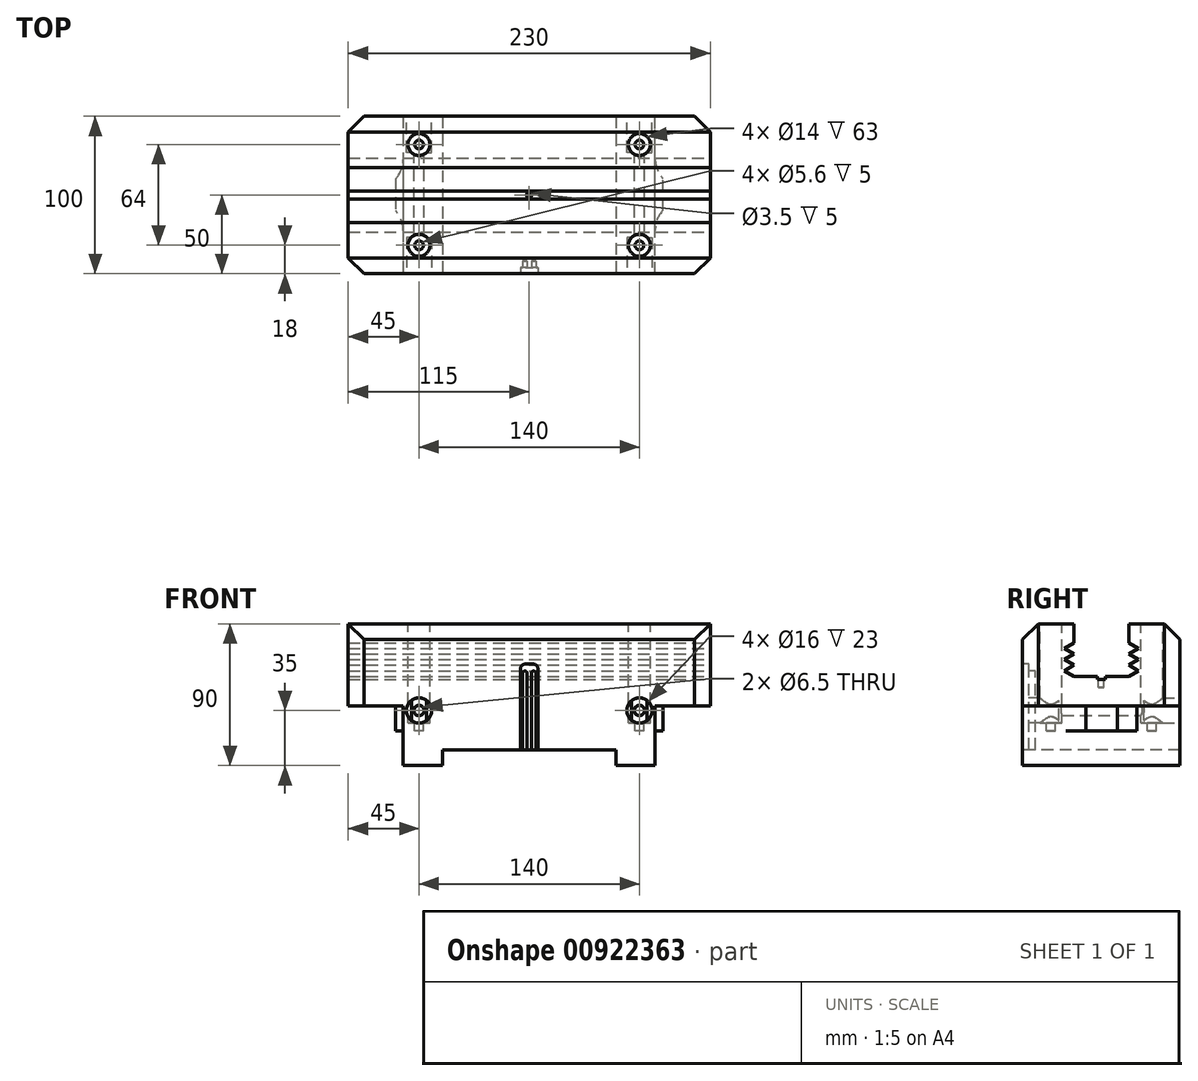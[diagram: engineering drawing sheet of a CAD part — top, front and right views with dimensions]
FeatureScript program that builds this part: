
annotation { "Feature Type Name" : "Feature", "Feature Type Description" : "" }
export const myFeature = defineFeature(function(context is Context, id is Id, definition is map)
    precondition{}
    {
        {
            var Q0;
            Q0=qCreatedBy(makeId("Top.planeOp"),FACE);
            var sketch = newSketch(context, id + "F0", { "sketchPlane" : qUnion([Q0])});
            skLineSegment(sketch, "E0.bottom", {"start": v(-115, 50) * mm, "end": v(115, 50) * mm});
            skLineSegment(sketch, "E0.top", {"start": v(-115, -50) * mm, "end": v(115, -50) * mm});
            skLineSegment(sketch, "E0.left", {"start": v(-115, 50) * mm, "end": v(-115, -50) * mm});
            skLineSegment(sketch, "E0.right", {"start": v(115, 50) * mm, "end": v(115, -50) * mm});
            skSolve(sketch);
        }
        {
            var Q0;
            Q0=makeQuery(id+"F0.imprint","IMPRINT",FACE,{"disambiguationData":[TD([[makeQuery(id+"F0.imprint","IMPRINT",EDGE,{"derivedFrom":sQuery(id+"F0.wireOp",EDGE,"E0.bottom")}),-1.0]])]});
            extrude(context, id + "F1", {"entities" : qUnion([Q0]), "oppositeDirection" : true, "depth" : 52 * mm, "offsetDistance" : 25 * mm});
        }
        {
            var Q0;
            Q0=makeQuery(id+"F1.opExtrude","SWEPT_FACE",FACE,{"disambiguationData":[OSD([sQuery(id+"F0.wireOp",EDGE,"E0.right")])]});
            var sketch = newSketch(context, id + "F2", { "sketchPlane" : qUnion([Q0])});
            skLineSegment(sketch, "E1", {"start": v(-17.5, 0) * mm, "end": v(17.5, 0) * mm});
            skLineSegment(sketch, "E2", {"start": v(-17.5, 0) * mm, "end": v(-17.5, -12) * mm});
            skLineSegment(sketch, "E3", {"start": v(-17.5, -12) * mm, "end": v(-23.52, -15.55) * mm});
            skLineSegment(sketch, "E4", {"start": v(-23.52, -15.55) * mm, "end": v(-17.5, -19.1) * mm});
            skLineSegment(sketch, "E5", {"start": v(-17.5, -19.1) * mm, "end": v(-23.52, -22.65) * mm});
            skLineSegment(sketch, "E6", {"start": v(-23.52, -22.65) * mm, "end": v(-17.5, -26.2) * mm});
            skLineSegment(sketch, "E7", {"start": v(-17.5, -26.2) * mm, "end": v(-23.52, -29.75) * mm});
            skLineSegment(sketch, "E8", {"start": v(-23.52, -29.75) * mm, "end": v(-17.5, -33.3) * mm});
            skLineSegment(sketch, "E9", {"start": v(17.5, 0) * mm, "end": v(17.5, -12) * mm});
            skLineSegment(sketch, "E10", {"start": v(17.5, -33.3) * mm, "end": v(23.52, -29.75) * mm});
            skLineSegment(sketch, "E11", {"start": v(23.52, -29.75) * mm, "end": v(17.5, -26.2) * mm});
            skLineSegment(sketch, "E12", {"start": v(17.5, -26.2) * mm, "end": v(23.52, -22.65) * mm});
            skLineSegment(sketch, "E13", {"start": v(23.52, -22.65) * mm, "end": v(17.5, -19.1) * mm});
            skLineSegment(sketch, "E14", {"start": v(17.5, -19.1) * mm, "end": v(23.52, -15.55) * mm});
            skLineSegment(sketch, "E15", {"start": v(23.52, -15.55) * mm, "end": v(17.5, -12) * mm});
            skLineSegment(sketch, "E16", {"start": v(-17.5, -33.3) * mm, "end": v(-2.5, -33.3) * mm});
            skLineSegment(sketch, "E17", {"start": v(17.5, -33.3) * mm, "end": v(2.5, -33.3) * mm});
            skLineSegment(sketch, "E18", {"start": v(-2.5, -33.3) * mm, "end": v(-2.5, -35.3) * mm});
            skLineSegment(sketch, "E19", {"start": v(2.5, -33.3) * mm, "end": v(2.5, -35.3) * mm});
            skLineSegment(sketch, "E20", {"start": v(2.5, -35.3) * mm, "end": v(-2.5, -35.3) * mm});
            skSolve(sketch);
        }
        {
            var Q0;
            Q0=makeQuery(id+"F2.imprint","IMPRINT",FACE,{"disambiguationData":[TD([[makeQuery(id+"F2.imprint","IMPRINT",EDGE,{"derivedFrom":sQuery(id+"F2.wireOp",EDGE,"E1")}),1.0]])]});
            extrude(context, id + "F3", {"entities" : qUnion([Q0]), "operationType" : NewBodyOperationType.REMOVE, "endBound" : BoundingType.UP_TO_NEXT, "oppositeDirection" : true, "depth" : 218 * mm, "offsetDistance" : 25 * mm});
        }
        {
            var Q0;
            Q0=makeQuery(id+"F1.opExtrude","CAP_EDGE",EDGE,{"disambiguationData":[OSD([sQuery(id+"F0.wireOp",EDGE,"E0.bottom")])],"isStart":true});
            var Q1;
            Q1=makeQuery(id+"F1.opExtrude","CAP_EDGE",EDGE,{"disambiguationData":[OSD([sQuery(id+"F0.wireOp",EDGE,"E0.top")])],"isStart":true});
            var Q2;
            Q2=makeQuery(id+"F1.opExtrude","SWEPT_EDGE",EDGE,{"disambiguationData":[OSD([sQuery(id+"F0.wireOp",EDGE,"E0.top"),sQuery(id+"F0.wireOp",EDGE,"E0.right")])]});
            var Q3;
            Q3=makeQuery(id+"F1.opExtrude","SWEPT_EDGE",EDGE,{"disambiguationData":[OSD([sQuery(id+"F0.wireOp",EDGE,"E0.bottom"),sQuery(id+"F0.wireOp",EDGE,"E0.right")])]});
            var Q4;
            Q4=makeQuery(id+"F1.opExtrude","SWEPT_EDGE",EDGE,{"disambiguationData":[OSD([sQuery(id+"F0.wireOp",EDGE,"E0.top"),sQuery(id+"F0.wireOp",EDGE,"E0.left")])]});
            var Q5;
            Q5=makeQuery(id+"F1.opExtrude","SWEPT_EDGE",EDGE,{"disambiguationData":[OSD([sQuery(id+"F0.wireOp",EDGE,"E0.bottom"),sQuery(id+"F0.wireOp",EDGE,"E0.left")])]});
            chamfer(context, id + "F4", {"entities" : qUnion([Q0, Q1, Q2, Q3, Q4, Q5]), "width" : 10 * mm, "tangentPropagation" : true});
        }
        {
            var Q0;
            Q0=makeQuery(id+"F1.opExtrude","CAP_FACE",FACE,{"disambiguationData":[OSD([sQuery(id+"F0.wireOp",EDGE,"E0.bottom"),sQuery(id+"F0.wireOp",EDGE,"E0.top"),sQuery(id+"F0.wireOp",EDGE,"E0.left"),sQuery(id+"F0.wireOp",EDGE,"E0.right")])],"isStart":false});
            var sketch = newSketch(context, id + "F5", { "sketchPlane" : qUnion([Q0])});
            skLineSegment(sketch, "E21", {"start": v(80, 50) * mm, "end": v(80, -50) * mm});
            skLineSegment(sketch, "E22", {"start": v(80, -50) * mm, "end": v(-80, -50) * mm});
            skLineSegment(sketch, "E23", {"start": v(-80, -50) * mm, "end": v(-80, 50) * mm});
            skLineSegment(sketch, "E24", {"start": v(-80, 50) * mm, "end": v(80, 50) * mm});
            skSolve(sketch);
        }
        {
            var Q0;
            Q0=makeQuery(id+"F5.imprint","IMPRINT",FACE,{"disambiguationData":[TD([[makeQuery(id+"F5.imprint","IMPRINT",EDGE,{"derivedFrom":sQuery(id+"F5.wireOp",EDGE,"E21")}),-1.0]])]});
            extrude(context, id + "F6", {"entities" : qUnion([Q0]), "operationType" : NewBodyOperationType.ADD, "depth" : 38 * mm, "offsetDistance" : 25 * mm});
        }
        {
            var Q0;
            {var subQ0=sQuery(id+"F0.wireOp",EDGE,"E0.bottom");var subQ1=sQuery(id+"F0.wireOp",EDGE,"E0.right");var subQ2=sQuery(id+"F0.wireOp",EDGE,"E0.left");Q0=makeQuery(id+"F3.boolean.opBoolean","SPLIT",FACE,{"disambiguationData":[TD([makeQuery(id+"F1.opExtrude","SWEPT_FACE",FACE,{"disambiguationData":[OSD([subQ0])]})])],"derivedFrom":makeQuery(id+"F1.opExtrude","CAP_FACE",FACE,{"disambiguationData":[OSD([subQ0,sQuery(id+"F0.wireOp",EDGE,"E0.top"),subQ2,subQ1])],"isStart":true})});}
            var sketch = newSketch(context, id + "F7", { "sketchPlane" : qUnion([Q0])});
            skCircle(sketch, "E25", {"center": v(70, -32) * mm, "radius": 7 * mm});
            skCircle(sketch, "E26", {"center": v(-70, -32) * mm, "radius": 7 * mm});
            skCircle(sketch, "E27", {"center": v(-70, 32) * mm, "radius": 7 * mm});
            skCircle(sketch, "E28", {"center": v(70, 32) * mm, "radius": 7 * mm});
            skCircle(sketch, "E29", {"center": v(-70, 32) * mm, "radius": 2.8 * mm});
            skCircle(sketch, "E30", {"center": v(70, 32) * mm, "radius": 2.8 * mm});
            skCircle(sketch, "E31", {"center": v(70, -32) * mm, "radius": 2.8 * mm});
            skCircle(sketch, "E32", {"center": v(-70, -32) * mm, "radius": 2.8 * mm});
            skSolve(sketch);
        }
        {
            var Q0;
            Q0=qSketchRegion(id+"F7",true);
            extrude(context, id + "F8", {"entities" : qUnion([Q0]), "operationType" : NewBodyOperationType.REMOVE, "oppositeDirection" : true, "depth" : 63 * mm, "offsetDistance" : 25 * mm});
        }
        {
            var Q0;
            {var subQ0=sQuery(id+"F0.wireOp",EDGE,"E0.bottom");var subQ1=sQuery(id+"F0.wireOp",EDGE,"E0.right");var subQ2=sQuery(id+"F0.wireOp",EDGE,"E0.left");Q0=makeQuery(id+"F8.boolean.opBoolean","SPLIT",FACE,{"disambiguationData":[TD([makeQuery(id+"F8.opExtrude","SWEPT_FACE",FACE,{"disambiguationData":[OSD([sQuery(id+"F7.wireOp",EDGE,"E30")])]})])],"derivedFrom":makeQuery(id+"F3.boolean.opBoolean","SPLIT",FACE,{"disambiguationData":[TD([makeQuery(id+"F1.opExtrude","SWEPT_FACE",FACE,{"disambiguationData":[OSD([subQ0])]})])],"derivedFrom":makeQuery(id+"F1.opExtrude","CAP_FACE",FACE,{"disambiguationData":[OSD([subQ0,sQuery(id+"F0.wireOp",EDGE,"E0.top"),subQ2,subQ1])],"isStart":true})})});}
            var Q1;
            {var subQ0=sQuery(id+"F0.wireOp",EDGE,"E0.bottom");var subQ1=sQuery(id+"F0.wireOp",EDGE,"E0.right");var subQ2=sQuery(id+"F0.wireOp",EDGE,"E0.left");Q1=makeQuery(id+"F8.boolean.opBoolean","SPLIT",FACE,{"disambiguationData":[TD([makeQuery(id+"F8.opExtrude","SWEPT_FACE",FACE,{"disambiguationData":[OSD([sQuery(id+"F7.wireOp",EDGE,"E29")])]})])],"derivedFrom":makeQuery(id+"F3.boolean.opBoolean","SPLIT",FACE,{"disambiguationData":[TD([makeQuery(id+"F1.opExtrude","SWEPT_FACE",FACE,{"disambiguationData":[OSD([subQ0])]})])],"derivedFrom":makeQuery(id+"F1.opExtrude","CAP_FACE",FACE,{"disambiguationData":[OSD([subQ0,sQuery(id+"F0.wireOp",EDGE,"E0.top"),subQ2,subQ1])],"isStart":true})})});}
            var Q2;
            {var subQ0=sQuery(id+"F0.wireOp",EDGE,"E0.top");var subQ1=sQuery(id+"F0.wireOp",EDGE,"E0.left");var subQ2=sQuery(id+"F0.wireOp",EDGE,"E0.right");Q2=makeQuery(id+"F8.boolean.opBoolean","SPLIT",FACE,{"disambiguationData":[TD([makeQuery(id+"F8.opExtrude","SWEPT_FACE",FACE,{"disambiguationData":[OSD([sQuery(id+"F7.wireOp",EDGE,"E32")])]})])],"derivedFrom":makeQuery(id+"F3.boolean.opBoolean","SPLIT",FACE,{"disambiguationData":[TD([makeQuery(id+"F1.opExtrude","SWEPT_FACE",FACE,{"disambiguationData":[OSD([subQ0])]})])],"derivedFrom":makeQuery(id+"F1.opExtrude","CAP_FACE",FACE,{"disambiguationData":[OSD([sQuery(id+"F0.wireOp",EDGE,"E0.bottom"),subQ0,subQ1,subQ2])],"isStart":true})})});}
            var Q3;
            {var subQ0=sQuery(id+"F0.wireOp",EDGE,"E0.top");var subQ1=sQuery(id+"F0.wireOp",EDGE,"E0.left");var subQ2=sQuery(id+"F0.wireOp",EDGE,"E0.right");Q3=makeQuery(id+"F8.boolean.opBoolean","SPLIT",FACE,{"disambiguationData":[TD([makeQuery(id+"F8.opExtrude","SWEPT_FACE",FACE,{"disambiguationData":[OSD([sQuery(id+"F7.wireOp",EDGE,"E31")])]})])],"derivedFrom":makeQuery(id+"F3.boolean.opBoolean","SPLIT",FACE,{"disambiguationData":[TD([makeQuery(id+"F1.opExtrude","SWEPT_FACE",FACE,{"disambiguationData":[OSD([subQ0])]})])],"derivedFrom":makeQuery(id+"F1.opExtrude","CAP_FACE",FACE,{"disambiguationData":[OSD([sQuery(id+"F0.wireOp",EDGE,"E0.bottom"),subQ0,subQ1,subQ2])],"isStart":true})})});}
            extrude(context, id + "F9", {"entities" : qUnion([Q0, Q1, Q2, Q3]), "operationType" : NewBodyOperationType.REMOVE, "oppositeDirection" : true, "depth" : 68 * mm, "offsetDistance" : 25 * mm});
        }
        {
            var Q0;
            Q0=makeQuery(id+"F6.boolean.opBoolean","MERGE",FACE,{"derivedFrom":[makeQuery(id+"F1.opExtrude","SWEPT_FACE",FACE,{"disambiguationData":[OSD([sQuery(id+"F0.wireOp",EDGE,"E0.bottom")])]}),makeQuery(id+"F6.opExtrude","SWEPT_FACE",FACE,{"disambiguationData":[OSD([sQuery(id+"F5.wireOp",EDGE,"E22")])]})]});
            var sketch = newSketch(context, id + "F10", { "sketchPlane" : qUnion([Q0])});
            skCircle(sketch, "E33", {"center": v(70, -55) * mm, "radius": 8 * mm});
            skCircle(sketch, "E34", {"center": v(-70, -55) * mm, "radius": 8 * mm});
            skCircle(sketch, "E35", {"center": v(70, -55) * mm, "radius": 3.25 * mm});
            skCircle(sketch, "E36", {"center": v(-70, -55) * mm, "radius": 3.25 * mm});
            skSolve(sketch);
        }
        {
            var Q0;
            Q0=qSketchRegion(id+"F10",true);
            extrude(context, id + "F11", {"entities" : qUnion([Q0]), "operationType" : NewBodyOperationType.REMOVE, "oppositeDirection" : true, "depth" : 23 * mm, "offsetDistance" : 25 * mm});
        }
        {
            var Q0;
            Q0=makeQuery(id+"F11.boolean.opBoolean","SPLIT",FACE,{"disambiguationData":[TD([makeQuery(id+"F11.opExtrude","SWEPT_FACE",FACE,{"disambiguationData":[OSD([sQuery(id+"F10.wireOp",EDGE,"E36")])]})])],"derivedFrom":makeQuery(id+"F6.boolean.opBoolean","MERGE",FACE,{"derivedFrom":[makeQuery(id+"F1.opExtrude","SWEPT_FACE",FACE,{"disambiguationData":[OSD([sQuery(id+"F0.wireOp",EDGE,"E0.bottom")])]}),makeQuery(id+"F6.opExtrude","SWEPT_FACE",FACE,{"disambiguationData":[OSD([sQuery(id+"F5.wireOp",EDGE,"E22")])]})]})});
            var Q1;
            Q1=makeQuery(id+"F11.boolean.opBoolean","SPLIT",FACE,{"disambiguationData":[TD([makeQuery(id+"F11.opExtrude","SWEPT_FACE",FACE,{"disambiguationData":[OSD([sQuery(id+"F10.wireOp",EDGE,"E35")])]})])],"derivedFrom":makeQuery(id+"F6.boolean.opBoolean","MERGE",FACE,{"derivedFrom":[makeQuery(id+"F1.opExtrude","SWEPT_FACE",FACE,{"disambiguationData":[OSD([sQuery(id+"F0.wireOp",EDGE,"E0.bottom")])]}),makeQuery(id+"F6.opExtrude","SWEPT_FACE",FACE,{"disambiguationData":[OSD([sQuery(id+"F5.wireOp",EDGE,"E22")])]})]})});
            extrude(context, id + "F12", {"entities" : qUnion([Q0, Q1]), "operationType" : NewBodyOperationType.REMOVE, "oppositeDirection" : true, "depth" : 179.1 * mm, "offsetDistance" : 25 * mm});
        }
        {
            var Q0;
            Q0=makeQuery(id+"F6.boolean.opBoolean","MERGE",FACE,{"derivedFrom":[makeQuery(id+"F1.opExtrude","SWEPT_FACE",FACE,{"disambiguationData":[OSD([sQuery(id+"F0.wireOp",EDGE,"E0.top")])]}),makeQuery(id+"F6.opExtrude","SWEPT_FACE",FACE,{"disambiguationData":[OSD([sQuery(id+"F5.wireOp",EDGE,"E24")])]})]});
            var sketch = newSketch(context, id + "F13", { "sketchPlane" : qUnion([Q0])});
            skCircle(sketch, "E37", {"center": v(-70, -55) * mm, "radius": 8 * mm});
            skCircle(sketch, "E38", {"center": v(-70, -55) * mm, "radius": 3.25 * mm});
            skCircle(sketch, "E39", {"center": v(70, -55) * mm, "radius": 8 * mm});
            skCircle(sketch, "E40", {"center": v(70, -55) * mm, "radius": 3.25 * mm});
            skLineSegment(sketch, "E41.bottom", {"start": v(-55, -90) * mm, "end": v(55, -90) * mm});
            skLineSegment(sketch, "E41.top", {"start": v(-55, -80) * mm, "end": v(55, -80) * mm});
            skLineSegment(sketch, "E41.left", {"start": v(-55, -90) * mm, "end": v(-55, -80) * mm});
            skLineSegment(sketch, "E41.right", {"start": v(55, -90) * mm, "end": v(55, -80) * mm});
            skSolve(sketch);
        }
        {
            var Q0;
            Q0=qSketchRegion(id+"F13",true);
            extrude(context, id + "F14", {"entities" : qUnion([Q0]), "operationType" : NewBodyOperationType.REMOVE, "oppositeDirection" : true, "depth" : 23 * mm, "offsetDistance" : 25 * mm});
        }
        {
            var Q0;
            Q0=makeQuery(id+"F13.imprint","IMPRINT",FACE,{"disambiguationData":[TD([[makeQuery(id+"F13.imprint","IMPRINT",EDGE,{"derivedFrom":sQuery(id+"F13.wireOp",EDGE,"E41.bottom")}),1.0]])]});
            extrude(context, id + "F15", {"entities" : qUnion([Q0]), "operationType" : NewBodyOperationType.REMOVE, "endBound" : BoundingType.THROUGH_ALL, "oppositeDirection" : true, "depth" : 25 * mm, "offsetDistance" : 25 * mm});
        }
        {
            var Q0;
            Q0=makeQuery(id+"F6.opExtrude","SWEPT_FACE",FACE,{"disambiguationData":[OSD([sQuery(id+"F5.wireOp",EDGE,"E23")])]});
            var sketch = newSketch(context, id + "F16", { "sketchPlane" : qUnion([Q0])});
            skLineSegment(sketch, "E42.bottom", {"start": v(-22.5, -52) * mm, "end": v(22.5, -52) * mm});
            skLineSegment(sketch, "E42.top", {"start": v(-22.5, -68) * mm, "end": v(22.5, -68) * mm});
            skLineSegment(sketch, "E42.left", {"start": v(-22.5, -52) * mm, "end": v(-22.5, -68) * mm});
            skLineSegment(sketch, "E42.right", {"start": v(22.5, -52) * mm, "end": v(22.5, -68) * mm});
            skSolve(sketch);
        }
        {
            var Q0;
            Q0=makeQuery(id+"F16.imprint","IMPRINT",FACE,{"disambiguationData":[TD([[makeQuery(id+"F16.imprint","IMPRINT",EDGE,{"derivedFrom":sQuery(id+"F16.wireOp",EDGE,"E42.bottom")}),-1.0]])]});
            extrude(context, id + "F17", {"entities" : qUnion([Q0]), "operationType" : NewBodyOperationType.ADD, "depth" : 5 * mm, "offsetDistance" : 25 * mm});
        }
        {
            var Q0;
            Q0=makeQuery(id+"F17.opExtrude","SWEPT_FACE",FACE,{"disambiguationData":[OSD([sQuery(id+"F16.wireOp",EDGE,"E42.top")])]});
            var sketch = newSketch(context, id + "F18", { "sketchPlane" : qUnion([Q0])});
            skLineSegment(sketch, "E43", {"start": v(-85, 10) * mm, "end": v(-85, -10) * mm});
            skArc(sketch, "E44", {"start": v(-80, -22.5) * mm, "mid": v(-81.3, -15.77) * mm, "end": v(-85, -10) * mm});
            skArc(sketch, "E45", {"start": v(-85, 10) * mm, "mid": v(-81.3, 15.77) * mm, "end": v(-80, 22.5) * mm});
            skSolve(sketch);
        }
        {
            var Q0;
            Q0=qSketchRegion(id+"F18",true);
            var Q1;
            {var subQ0=sQuery(id+"F18.wireOp",EDGE,"E44");Q1=makeQuery(id+"F18.imprint","IMPRINT",FACE,{"disambiguationData":[TD([[makeQuery(id+"F18.imprint","IMPRINT",EDGE,{"derivedFrom":subQ0}),1.0]])]});}
            var Q2;
            {var subQ0=sQuery(id+"F18.wireOp",EDGE,"E45");Q2=makeQuery(id+"F18.imprint","IMPRINT",FACE,{"disambiguationData":[TD([[makeQuery(id+"F18.imprint","IMPRINT",EDGE,{"derivedFrom":subQ0}),1.0]])]});}
            extrude(context, id + "F19", {"entities" : qUnion([Q0, Q1, Q2]), "operationType" : NewBodyOperationType.REMOVE, "oppositeDirection" : true, "depth" : 16 * mm, "offsetDistance" : 25 * mm});
        }
        {
            var Q0;
            Q0=makeQuery(id+"F6.opExtrude","SWEPT_FACE",FACE,{"disambiguationData":[OSD([sQuery(id+"F5.wireOp",EDGE,"E21")])]});
            var sketch = newSketch(context, id + "F20", { "sketchPlane" : qUnion([Q0])});
            skLineSegment(sketch, "E46.bottom", {"start": v(-22.5, -52) * mm, "end": v(22.5, -52) * mm});
            skLineSegment(sketch, "E46.top", {"start": v(-22.5, -68) * mm, "end": v(22.5, -68) * mm});
            skLineSegment(sketch, "E46.left", {"start": v(-22.5, -52) * mm, "end": v(-22.5, -68) * mm});
            skLineSegment(sketch, "E46.right", {"start": v(22.5, -52) * mm, "end": v(22.5, -68) * mm});
            skSolve(sketch);
        }
        {
            var Q0;
            Q0=makeQuery(id+"F20.imprint","IMPRINT",FACE,{"disambiguationData":[TD([[makeQuery(id+"F20.imprint","IMPRINT",EDGE,{"derivedFrom":sQuery(id+"F20.wireOp",EDGE,"E46.bottom")}),-1.0]])]});
            extrude(context, id + "F21", {"entities" : qUnion([Q0]), "operationType" : NewBodyOperationType.ADD, "depth" : 5 * mm, "offsetDistance" : 25 * mm});
        }
        {
            var Q0;
            Q0=makeQuery(id+"F21.opExtrude","SWEPT_FACE",FACE,{"disambiguationData":[OSD([sQuery(id+"F20.wireOp",EDGE,"E46.top")])]});
            var sketch = newSketch(context, id + "F22", { "sketchPlane" : qUnion([Q0])});
            skLineSegment(sketch, "E47", {"start": v(85, -10.3) * mm, "end": v(85, 9.7) * mm});
            skArc(sketch, "E48", {"start": v(80, 22.5) * mm, "mid": v(81.3, 15.63) * mm, "end": v(85, 9.7) * mm});
            skArc(sketch, "E49", {"start": v(85, -10.3) * mm, "mid": v(81.35, -15.93) * mm, "end": v(80, -22.5) * mm});
            skSolve(sketch);
        }
        {
            var Q0;
            Q0=qSketchRegion(id+"F22",true);
            var Q1;
            {var subQ0=sQuery(id+"F22.wireOp",EDGE,"E49");Q1=makeQuery(id+"F22.imprint","IMPRINT",FACE,{"disambiguationData":[TD([[makeQuery(id+"F22.imprint","IMPRINT",EDGE,{"derivedFrom":subQ0}),1.0]])]});}
            var Q2;
            {var subQ0=sQuery(id+"F22.wireOp",EDGE,"E48");Q2=makeQuery(id+"F22.imprint","IMPRINT",FACE,{"disambiguationData":[TD([[makeQuery(id+"F22.imprint","IMPRINT",EDGE,{"derivedFrom":subQ0}),1.0]])]});}
            extrude(context, id + "F23", {"entities" : qUnion([Q0, Q1, Q2]), "operationType" : NewBodyOperationType.REMOVE, "oppositeDirection" : true, "depth" : 16 * mm, "offsetDistance" : 25 * mm});
        }
        {
            var Q0;
            Q0=makeQuery(id+"F6.boolean.opBoolean","MERGE",FACE,{"derivedFrom":[makeQuery(id+"F1.opExtrude","SWEPT_FACE",FACE,{"disambiguationData":[OSD([sQuery(id+"F0.wireOp",EDGE,"E0.top")])]}),makeQuery(id+"F6.opExtrude","SWEPT_FACE",FACE,{"disambiguationData":[OSD([sQuery(id+"F5.wireOp",EDGE,"E24")])]})]});
            var sketch = newSketch(context, id + "F24", { "sketchPlane" : qUnion([Q0])});
            skLineSegment(sketch, "E50.bottom", {"start": v(-5.5, -80) * mm, "end": v(5.5, -80) * mm});
            skLineSegment(sketch, "E50.left", {"start": v(-5.5, -80) * mm, "end": v(-5.5, -31) * mm});
            skLineSegment(sketch, "E50.right", {"start": v(5.5, -80) * mm, "end": v(5.5, -31) * mm});
            skLineSegment(sketch, "E51.top", {"start": v(-2.5, -25.5) * mm, "end": v(2.5, -25.5) * mm});
            skLineSegment(sketch, "E51.left", {"start": v(-5.5, -31) * mm, "end": v(-5.5, -28.5) * mm});
            skLineSegment(sketch, "E51.right", {"start": v(5.5, -31) * mm, "end": v(5.5, -28.5) * mm});
            skPoint(sketch, "E52.visualSharp", {"position": v(5.5, -25.5) * mm});
            skArc(sketch, "E52.filletArc", {"start": v(5.5, -28.5) * mm, "mid": v(4.62, -26.38) * mm, "end": v(2.5, -25.5) * mm});
            skPoint(sketch, "E53.visualSharp", {"position": v(-5.5, -25.5) * mm});
            skArc(sketch, "E53.filletArc", {"start": v(-2.5, -25.5) * mm, "mid": v(-4.62, -26.38) * mm, "end": v(-5.5, -28.5) * mm});
            skSolve(sketch);
        }
        {
            var Q0;
            Q0=makeQuery(id+"F24.imprint","IMPRINT",FACE,{"disambiguationData":[TD([[makeQuery(id+"F24.imprint","IMPRINT",EDGE,{"derivedFrom":sQuery(id+"F24.wireOp",EDGE,"E50.bottom")}),1.0]])]});
            extrude(context, id + "F25", {"entities" : qUnion([Q0]), "operationType" : NewBodyOperationType.REMOVE, "oppositeDirection" : true, "depth" : 4 * mm, "offsetDistance" : 25 * mm});
        }
        {
            var Q0;
            Q0=makeQuery(id+"F25.boolean.opBoolean","COPY",FACE,{"derivedFrom":makeQuery(id+"F25.opExtrude","CAP_FACE",FACE,{"disambiguationData":[OSD([sQuery(id+"F24.wireOp",EDGE,"E50.bottom"),sQuery(id+"F24.wireOp",EDGE,"E50.left"),sQuery(id+"F24.wireOp",EDGE,"E50.right"),sQuery(id+"F24.wireOp",EDGE,"E51.top"),sQuery(id+"F24.wireOp",EDGE,"E51.left"),sQuery(id+"F24.wireOp",EDGE,"E51.right"),sQuery(id+"F24.wireOp",EDGE,"E52.filletArc"),sQuery(id+"F24.wireOp",EDGE,"E53.filletArc")])],"isStart":false})});
            var sketch = newSketch(context, id + "F26", { "sketchPlane" : qUnion([Q0])});
            skLineSegment(sketch, "E54.bottom", {"start": v(1.3, -80) * mm, "end": v(4.3, -80) * mm});
            skLineSegment(sketch, "E54.left", {"start": v(1.3, -80) * mm, "end": v(1.3, -31.5) * mm});
            skLineSegment(sketch, "E54.right", {"start": v(4.3, -80) * mm, "end": v(4.3, -31.5) * mm});
            skLineSegment(sketch, "E55.bottom", {"start": v(-4.3, -80) * mm, "end": v(-1.3, -80) * mm});
            skLineSegment(sketch, "E55.left", {"start": v(-4.3, -80) * mm, "end": v(-4.3, -31.5) * mm});
            skLineSegment(sketch, "E55.right", {"start": v(-1.3, -80) * mm, "end": v(-1.3, -31.5) * mm});
            skArc(sketch, "E56", {"start": v(4.3, -31.5) * mm, "mid": v(2.8, -30) * mm, "end": v(1.3, -31.5) * mm});
            skArc(sketch, "E57", {"start": v(-1.3, -31.5) * mm, "mid": v(-2.8, -30) * mm, "end": v(-4.3, -31.5) * mm});
            skSolve(sketch);
        }
        {
            var Q0;
            Q0=qSketchRegion(id+"F26",true);
            extrude(context, id + "F27", {"entities" : qUnion([Q0]), "operationType" : NewBodyOperationType.REMOVE, "oppositeDirection" : true, "depth" : 4 * mm, "offsetDistance" : 25 * mm});
        }
        {
            var Q0;
            Q0=makeQuery(id+"F3.boolean.opBoolean","COPY",FACE,{"derivedFrom":makeQuery(id+"F3.opExtrude","SWEPT_FACE",FACE,{"disambiguationData":[OSD([sQuery(id+"F2.wireOp",EDGE,"E20")])]})});
            var sketch = newSketch(context, id + "F28", { "sketchPlane" : qUnion([Q0])});
            skCircle(sketch, "E58", {"center": v(0, 0) * mm, "radius": 1.75 * mm});
            skSolve(sketch);
        }
        {
            var Q0;
            Q0=qSketchRegion(id+"F28",true);
            extrude(context, id + "F29", {"entities" : qUnion([Q0]), "operationType" : NewBodyOperationType.REMOVE, "oppositeDirection" : true, "depth" : 5 * mm, "offsetDistance" : 25 * mm});
        }
    });
